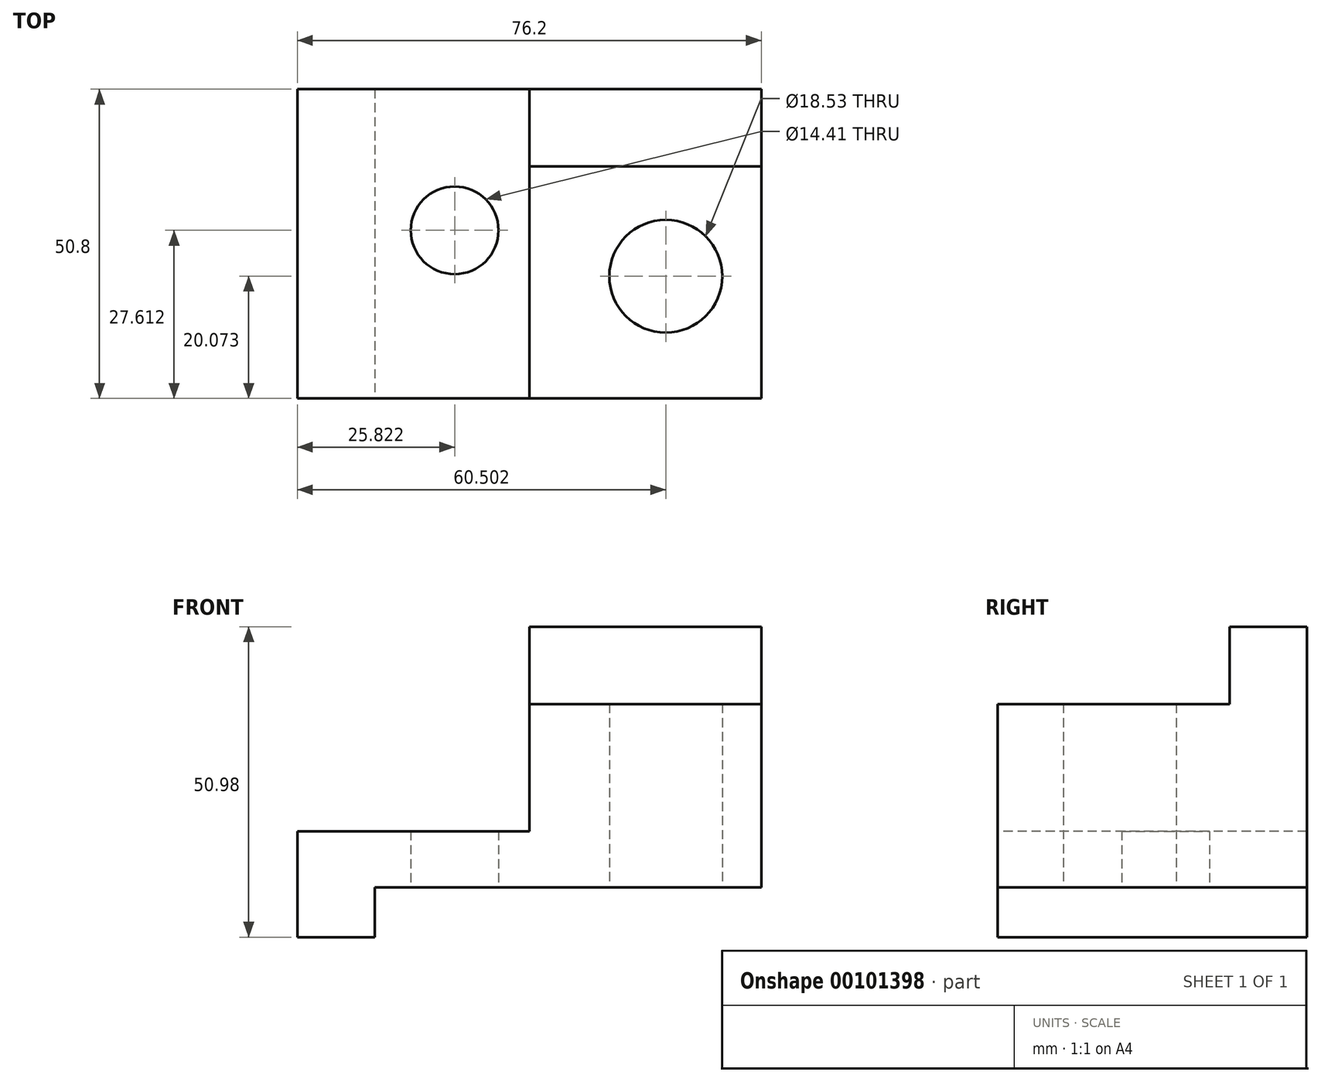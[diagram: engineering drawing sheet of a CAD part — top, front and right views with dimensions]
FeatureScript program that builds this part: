
annotation { "Feature Type Name" : "Feature", "Feature Type Description" : "" }
export const myFeature = defineFeature(function(context is Context, id is Id, definition is map)
    precondition{}
    {
        {
            var Q0;
            Q0=qCreatedBy(makeId("Front.planeOp"),FACE);
            var sketch = newSketch(context, id + "F0", { "sketchPlane" : qUnion([Q0])});
            skLineSegment(sketch, "E0", {"start": v(12.7, 0) * mm, "end": v(12.7, 8.14) * mm});
            skLineSegment(sketch, "E1", {"start": v(12.7, 8.14) * mm, "end": v(76.2, 8.14) * mm});
            skLineSegment(sketch, "E2", {"start": v(0, 17.4) * mm, "end": v(38.1, 17.4) * mm});
            skLineSegment(sketch, "E3", {"start": v(38.1, 17.4) * mm, "end": v(38.1, 50.8) * mm});
            skLineSegment(sketch, "E4", {"start": v(0, 17.4) * mm, "end": v(0, 0) * mm});
            skLineSegment(sketch, "E5", {"start": v(0, 0) * mm, "end": v(12.7, 0) * mm});
            skLineSegment(sketch, "E6", {"start": v(76.2, 8.14) * mm, "end": v(76.2, 50.98) * mm});
            skLineSegment(sketch, "E7", {"start": v(76.2, 50.98) * mm, "end": v(38.1, 50.8) * mm});
            skSolve(sketch);
        }
        {
            var Q0;
            Q0=qCreatedBy(makeId("Top.planeOp"),FACE);
            var sketch = newSketch(context, id + "F1", { "sketchPlane" : qUnion([Q0])});
            skCircle(sketch, "E8", {"center": v(25.82, 27.61) * mm, "radius": 7.2 * mm});
            skCircle(sketch, "E9", {"center": v(60.5, 20.07) * mm, "radius": 9.27 * mm});
            skSolve(sketch);
        }
        {
            var Q0;
            Q0 = qSketchRegion(id + "F0", true);
            extrude(context, id + "F2", {"entities" : qUnion([Q0]), "oppositeDirection" : true, "depth" : 50.8 * mm});
        }
        {
            var Q0;
            Q0 = qSketchRegion(id + "F1", true);
            extrude(context, id + "F3", {"entities" : qUnion([Q0]), "operationType" : NewBodyOperationType.REMOVE, "depth" : 88.9 * mm});
        }
        {
            var Q0;
            Q0=makeQuery(id+"F2.opExtrude","SWEPT_FACE",FACE,{"disambiguationData":[OSD([sQuery(id+"F0.wireOp",EDGE,"E6")])]});
            var sketch = newSketch(context, id + "F4", { "sketchPlane" : qUnion([Q0])});
            skLineSegment(sketch, "E10", {"start": v(50.8, 38.28) * mm, "end": v(50.8, 50.98) * mm});
            skLineSegment(sketch, "E11", {"start": v(38.1, 50.98) * mm, "end": v(38.1, 38.28) * mm});
            skLineSegment(sketch, "E12", {"start": v(38.1, 38.28) * mm, "end": v(50.8, 38.28) * mm});
            skLineSegment(sketch, "E13", {"start": v(38.1, 50.98) * mm, "end": v(50.8, 50.98) * mm});
            skSolve(sketch);
        }
        {
            var Q0;
            Q0 = qSketchRegion(id + "F4", true);
            extrude(context, id + "F5", {"entities" : qUnion([Q0]), "operationType" : NewBodyOperationType.ADD, "oppositeDirection" : true, "depth" : 38.1 * mm});
        }
        {
            var Q0;
            Q0=qCreatedBy(makeId("Right.planeOp"),FACE);
            var sketch = newSketch(context, id + "F6", { "sketchPlane" : qUnion([Q0])});
            skLineSegment(sketch, "E14", {"start": v(0, 50.98) * mm, "end": v(0, 38.28) * mm});
            skLineSegment(sketch, "E15", {"start": v(0, 38.28) * mm, "end": v(38.1, 38.28) * mm});
            skLineSegment(sketch, "E16", {"start": v(38.1, 38.28) * mm, "end": v(38.1, 51.34) * mm});
            skLineSegment(sketch, "E17", {"start": v(38.1, 51.34) * mm, "end": v(0, 50.98) * mm});
            skLineSegment(sketch, "E18", {"start": v(0, 50.98) * mm, "end": v(0, 0) * mm});
            skLineSegment(sketch, "E19", {"start": v(0, 0) * mm, "end": v(48.63, 0.46) * mm});
            skSolve(sketch);
        }
        {
            var Q0;
            Q0 = qSketchRegion(id + "F6", true);
            extrude(context, id + "F7", {"entities" : qUnion([Q0]), "operationType" : NewBodyOperationType.REMOVE, "depth" : 76.2 * mm});
        }
    });
